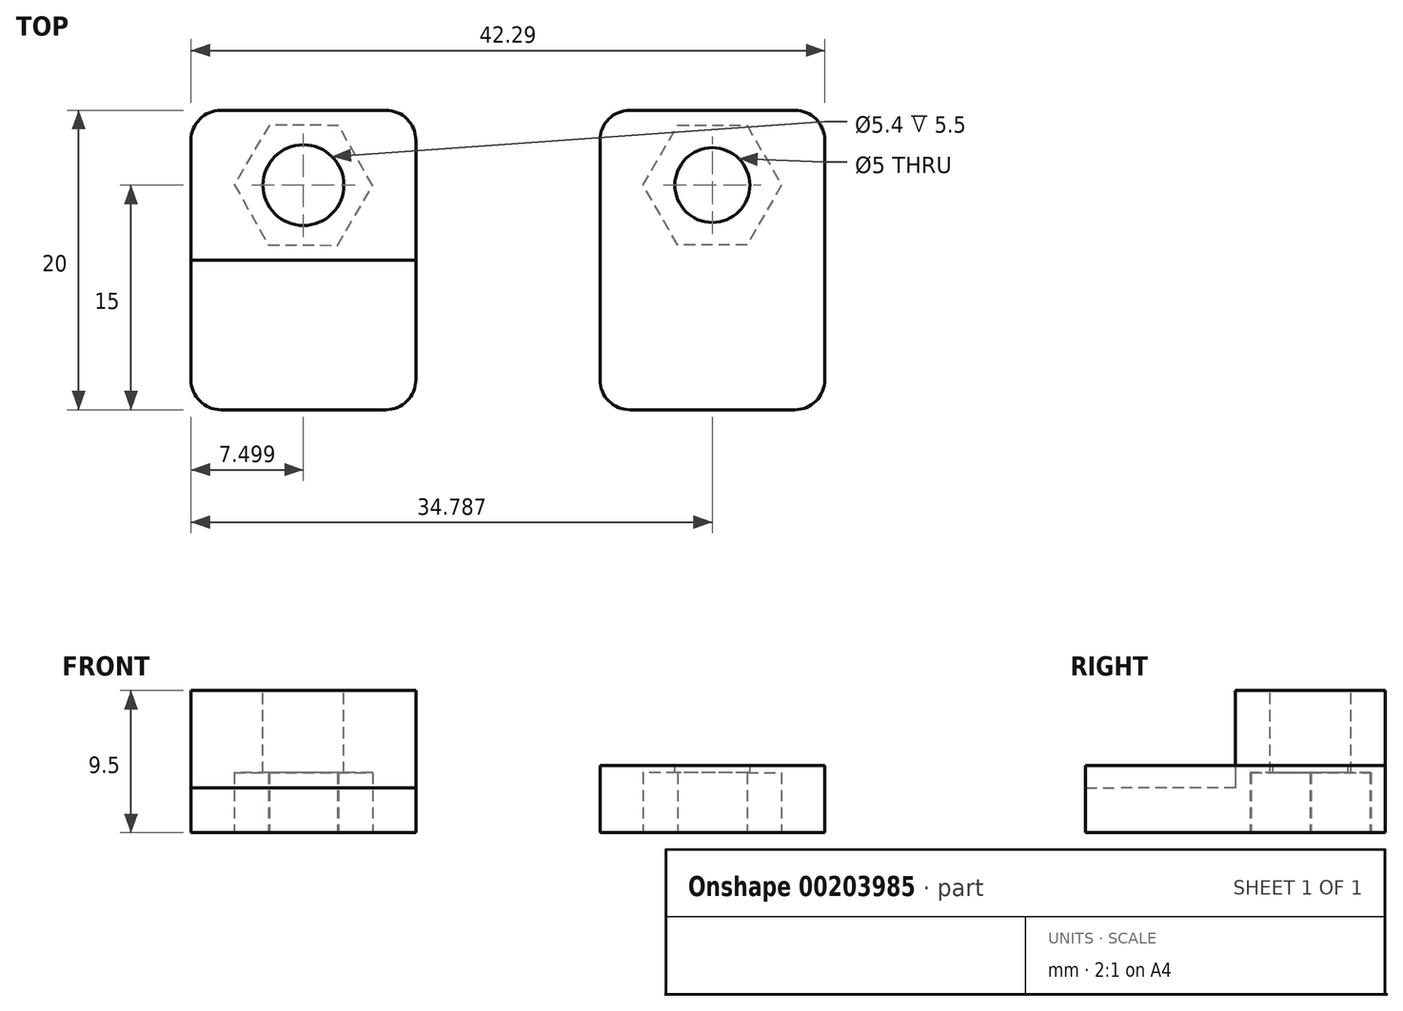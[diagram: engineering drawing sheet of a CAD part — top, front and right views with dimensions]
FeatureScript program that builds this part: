
annotation { "Feature Type Name" : "Feature", "Feature Type Description" : "" }
export const myFeature = defineFeature(function(context is Context, id is Id, definition is map)
    precondition{}
    {
        {
            var Q0;
            Q0=qCreatedBy(makeId("Top.planeOp"),FACE);
            var sketch = newSketch(context, id + "F0", { "sketchPlane" : qUnion([Q0])});
            skLineSegment(sketch, "E0.bottom", {"start": v(-45.3, 10) * mm, "end": v(-30.3, 10) * mm});
            skLineSegment(sketch, "E0.top", {"start": v(-45.3, -10) * mm, "end": v(-30.3, -10) * mm});
            skLineSegment(sketch, "E0.left", {"start": v(-45.3, 10) * mm, "end": v(-45.3, -10) * mm});
            skLineSegment(sketch, "E0.right", {"start": v(-30.3, 10) * mm, "end": v(-30.3, -10) * mm});
            skSolve(sketch);
        }
        {
            var Q0;
            Q0=makeQuery(id+"F0.imprint","IMPRINT",FACE,{"disambiguationData":[TD([[makeQuery(id+"F0.imprint","IMPRINT",EDGE,{"derivedFrom":sQuery(id+"F0.wireOp",EDGE,"E0.bottom")}),-1.0]])]});
            extrude(context, id + "F1", {"entities" : qUnion([Q0]), "depth" : 3 * mm});
        }
        {
            var Q0;
            Q0=makeQuery(id+"F1.opExtrude","CAP_FACE",FACE,{"disambiguationData":[OSD([sQuery(id+"F0.wireOp",EDGE,"E0.bottom"),sQuery(id+"F0.wireOp",EDGE,"E0.top"),sQuery(id+"F0.wireOp",EDGE,"E0.left"),sQuery(id+"F0.wireOp",EDGE,"E0.right")])],"isStart":false});
            var sketch = newSketch(context, id + "F2", { "sketchPlane" : qUnion([Q0])});
            skLineSegment(sketch, "E1.bottom", {"start": v(-45.3, 10) * mm, "end": v(-30.3, 10) * mm});
            skLineSegment(sketch, "E1.top", {"start": v(-45.3, 0) * mm, "end": v(-30.3, 0) * mm});
            skLineSegment(sketch, "E1.left", {"start": v(-45.3, 10) * mm, "end": v(-45.3, 0) * mm});
            skLineSegment(sketch, "E1.right", {"start": v(-30.3, 10) * mm, "end": v(-30.3, 0) * mm});
            skSolve(sketch);
        }
        {
            var Q0;
            Q0=makeQuery(id+"F2.imprint","IMPRINT",FACE,{"disambiguationData":[TD([[makeQuery(id+"F2.imprint","IMPRINT",EDGE,{"derivedFrom":sQuery(id+"F2.wireOp",EDGE,"E1.bottom")}),-1.0]])]});
            extrude(context, id + "F3", {"entities" : qUnion([Q0]), "operationType" : NewBodyOperationType.ADD, "depth" : 6.5 * mm});
        }
        {
            var Q0;
            Q0=makeQuery(id+"F3.opExtrude","CAP_FACE",FACE,{"disambiguationData":[OSD([sQuery(id+"F2.wireOp",EDGE,"E1.bottom"),sQuery(id+"F2.wireOp",EDGE,"E1.top"),sQuery(id+"F2.wireOp",EDGE,"E1.left"),sQuery(id+"F2.wireOp",EDGE,"E1.right")])],"isStart":false});
            var sketch = newSketch(context, id + "F4", { "sketchPlane" : qUnion([Q0])});
            skCircle(sketch, "E2", {"center": v(-37.8, 5) * mm, "radius": 2.7 * mm});
            skPoint(sketch, "E2.centerSnap0", {"position": v(-37.8, 10) * mm});
            skSolve(sketch);
        }
        {
            var Q0;
            Q0=makeQuery(id+"F4.imprint","IMPRINT",FACE,{"disambiguationData":[TD([[makeQuery(id+"F4.imprint","IMPRINT",EDGE,{"derivedFrom":sQuery(id+"F4.wireOp",EDGE,"E2")}),1.0]])]});
            extrude(context, id + "F5", {"entities" : qUnion([Q0]), "operationType" : NewBodyOperationType.REMOVE, "oppositeDirection" : true, "depth" : 25 * mm});
        }
        {
            var Q0;
            Q0=makeQuery(id+"F1.opExtrude","SWEPT_EDGE",EDGE,{"disambiguationData":[OSD([sQuery(id+"F0.wireOp",EDGE,"E0.top"),sQuery(id+"F0.wireOp",EDGE,"E0.left")])]});
            var Q1;
            Q1=makeQuery(id+"F1.opExtrude","SWEPT_EDGE",EDGE,{"disambiguationData":[OSD([sQuery(id+"F0.wireOp",EDGE,"E0.top"),sQuery(id+"F0.wireOp",EDGE,"E0.right")])]});
            var Q2;
            Q2=makeQuery(id+"F3.boolean.opBoolean","MERGE",EDGE,{"derivedFrom":[makeQuery(id+"F1.opExtrude","SWEPT_EDGE",EDGE,{"disambiguationData":[OSD([sQuery(id+"F0.wireOp",EDGE,"E0.bottom"),sQuery(id+"F0.wireOp",EDGE,"E0.right")])]}),makeQuery(id+"F3.opExtrude","SWEPT_EDGE",EDGE,{"disambiguationData":[OSD([sQuery(id+"F2.wireOp",EDGE,"E1.bottom"),sQuery(id+"F2.wireOp",EDGE,"E1.right")])]})]});
            var Q3;
            Q3=makeQuery(id+"F3.boolean.opBoolean","MERGE",EDGE,{"derivedFrom":[makeQuery(id+"F1.opExtrude","SWEPT_EDGE",EDGE,{"disambiguationData":[OSD([sQuery(id+"F0.wireOp",EDGE,"E0.bottom"),sQuery(id+"F0.wireOp",EDGE,"E0.left")])]}),makeQuery(id+"F3.opExtrude","SWEPT_EDGE",EDGE,{"disambiguationData":[OSD([sQuery(id+"F2.wireOp",EDGE,"E1.bottom"),sQuery(id+"F2.wireOp",EDGE,"E1.left")])]})]});
            fillet(context, id + "F6", {"entities" : qUnion([Q0, Q1, Q2, Q3]), "radius" : 2 * mm, "tangentPropagation" : true, "allowEdgeOverflow" : false});
        }
        {
            var Q0;
            Q0=qCreatedBy(makeId("Top.planeOp"),FACE);
            var sketch = newSketch(context, id + "F7", { "sketchPlane" : qUnion([Q0])});
            skLineSegment(sketch, "E3.bottom", {"start": v(-18.01, 10) * mm, "end": v(-3.01, 10) * mm});
            skLineSegment(sketch, "E3.top", {"start": v(-18.01, -10) * mm, "end": v(-3.01, -10) * mm});
            skLineSegment(sketch, "E3.left", {"start": v(-18.01, 10) * mm, "end": v(-18.01, -10) * mm});
            skLineSegment(sketch, "E3.right", {"start": v(-3.01, 10) * mm, "end": v(-3.01, -10) * mm});
            skSolve(sketch);
        }
        {
            var Q0;
            Q0=makeQuery(id+"F7.imprint","IMPRINT",FACE,{"disambiguationData":[TD([[makeQuery(id+"F7.imprint","IMPRINT",EDGE,{"derivedFrom":sQuery(id+"F7.wireOp",EDGE,"E3.bottom")}),-1.0]])]});
            extrude(context, id + "F8", {"entities" : qUnion([Q0]), "depth" : 4.5 * mm});
        }
        {
            var Q0;
            Q0=makeQuery(id+"F8.opExtrude","CAP_FACE",FACE,{"disambiguationData":[OSD([sQuery(id+"F7.wireOp",EDGE,"E3.bottom"),sQuery(id+"F7.wireOp",EDGE,"E3.top"),sQuery(id+"F7.wireOp",EDGE,"E3.left"),sQuery(id+"F7.wireOp",EDGE,"E3.right")])],"isStart":false});
            var sketch = newSketch(context, id + "F9", { "sketchPlane" : qUnion([Q0])});
            skCircle(sketch, "E4", {"center": v(-10.51, 5) * mm, "radius": 2.5 * mm});
            skSolve(sketch);
        }
        {
            var Q0;
            Q0=makeQuery(id+"F9.imprint","IMPRINT",FACE,{"disambiguationData":[TD([[makeQuery(id+"F9.imprint","IMPRINT",EDGE,{"derivedFrom":sQuery(id+"F9.wireOp",EDGE,"E4")}),1.0]])]});
            extrude(context, id + "F10", {"entities" : qUnion([Q0]), "operationType" : NewBodyOperationType.REMOVE, "oppositeDirection" : true, "depth" : 25 * mm});
        }
        {
            var Q0;
            Q0=makeQuery(id+"F8.opExtrude","SWEPT_EDGE",EDGE,{"disambiguationData":[OSD([sQuery(id+"F7.wireOp",EDGE,"E3.bottom"),sQuery(id+"F7.wireOp",EDGE,"E3.left")])]});
            var Q1;
            Q1=makeQuery(id+"F8.opExtrude","SWEPT_EDGE",EDGE,{"disambiguationData":[OSD([sQuery(id+"F7.wireOp",EDGE,"E3.top"),sQuery(id+"F7.wireOp",EDGE,"E3.left")])]});
            var Q2;
            Q2=makeQuery(id+"F8.opExtrude","SWEPT_EDGE",EDGE,{"disambiguationData":[OSD([sQuery(id+"F7.wireOp",EDGE,"E3.top"),sQuery(id+"F7.wireOp",EDGE,"E3.right")])]});
            var Q3;
            Q3=makeQuery(id+"F8.opExtrude","SWEPT_EDGE",EDGE,{"disambiguationData":[OSD([sQuery(id+"F7.wireOp",EDGE,"E3.bottom"),sQuery(id+"F7.wireOp",EDGE,"E3.right")])]});
            fillet(context, id + "F11", {"entities" : qUnion([Q0, Q1, Q2, Q3]), "radius" : 2 * mm, "tangentPropagation" : true, "allowEdgeOverflow" : false});
        }
        {
            var Q0;
            Q0=makeQuery(id+"F1.opExtrude","CAP_FACE",FACE,{"disambiguationData":[OSD([sQuery(id+"F0.wireOp",EDGE,"E0.bottom"),sQuery(id+"F0.wireOp",EDGE,"E0.top"),sQuery(id+"F0.wireOp",EDGE,"E0.left"),sQuery(id+"F0.wireOp",EDGE,"E0.right")])],"isStart":true});
            var sketch = newSketch(context, id + "F12", { "sketchPlane" : qUnion([Q0])});
            skCircle(sketch, "E5.cCircle", {"center": v(-37.8, -5) * mm, "radius": 4 * mm, "construction": true});
            skLineSegment(sketch, "E5.0", {"start": v(-40.08, -9.02) * mm, "end": v(-42.42, -5.04) * mm});
            skLineSegment(sketch, "E5.1", {"start": v(-42.42, -5.04) * mm, "end": v(-40.14, -1.02) * mm});
            skLineSegment(sketch, "E5.2", {"start": v(-40.14, -1.02) * mm, "end": v(-35.53, -0.98) * mm});
            skLineSegment(sketch, "E5.3", {"start": v(-35.53, -0.98) * mm, "end": v(-33.18, -4.96) * mm});
            skLineSegment(sketch, "E5.4", {"start": v(-33.18, -4.96) * mm, "end": v(-35.46, -8.98) * mm});
            skLineSegment(sketch, "E5.5", {"start": v(-35.46, -8.98) * mm, "end": v(-40.08, -9.02) * mm});
            skPoint(sketch, "E5.0.midPoint", {"position": v(-41.25, -7.03) * mm});
            skSolve(sketch);
        }
        {
            var Q0;
            Q0=makeQuery(id+"F12.imprint","IMPRINT",FACE,{"disambiguationData":[TD([[makeQuery(id+"F12.imprint","IMPRINT",EDGE,{"derivedFrom":sQuery(id+"F12.wireOp",EDGE,"E5.0")}),-1.0]])]});
            extrude(context, id + "F13", {"entities" : qUnion([Q0]), "operationType" : NewBodyOperationType.REMOVE, "oppositeDirection" : true, "depth" : 4 * mm});
        }
        {
            var Q0;
            Q0=qCreatedBy(makeId("Top.planeOp"),FACE);
            var sketch = newSketch(context, id + "F14", { "sketchPlane" : qUnion([Q0])});
            skCircle(sketch, "E6.cCircle", {"center": v(-10.51, 5) * mm, "radius": 4 * mm, "construction": true});
            skLineSegment(sketch, "E6.0", {"start": v(-8.2, 1) * mm, "end": v(-12.82, 1) * mm});
            skLineSegment(sketch, "E6.1", {"start": v(-12.82, 1) * mm, "end": v(-15.13, 5) * mm});
            skLineSegment(sketch, "E6.2", {"start": v(-15.13, 5) * mm, "end": v(-12.82, 9) * mm});
            skLineSegment(sketch, "E6.3", {"start": v(-12.82, 9) * mm, "end": v(-8.2, 9) * mm});
            skLineSegment(sketch, "E6.4", {"start": v(-8.2, 9) * mm, "end": v(-5.9, 5) * mm});
            skLineSegment(sketch, "E6.5", {"start": v(-5.9, 5) * mm, "end": v(-8.2, 1) * mm});
            skPoint(sketch, "E6.0.midPoint", {"position": v(-10.51, 1) * mm});
            skSolve(sketch);
        }
        {
            var Q0;
            Q0=makeQuery(id+"F14.imprint","IMPRINT",FACE,{"disambiguationData":[TD([[makeQuery(id+"F14.imprint","IMPRINT",EDGE,{"derivedFrom":sQuery(id+"F14.wireOp",EDGE,"E6.0")}),-1.0]])]});
            extrude(context, id + "F15", {"entities" : qUnion([Q0]), "operationType" : NewBodyOperationType.REMOVE, "depth" : 4 * mm});
        }
    });
